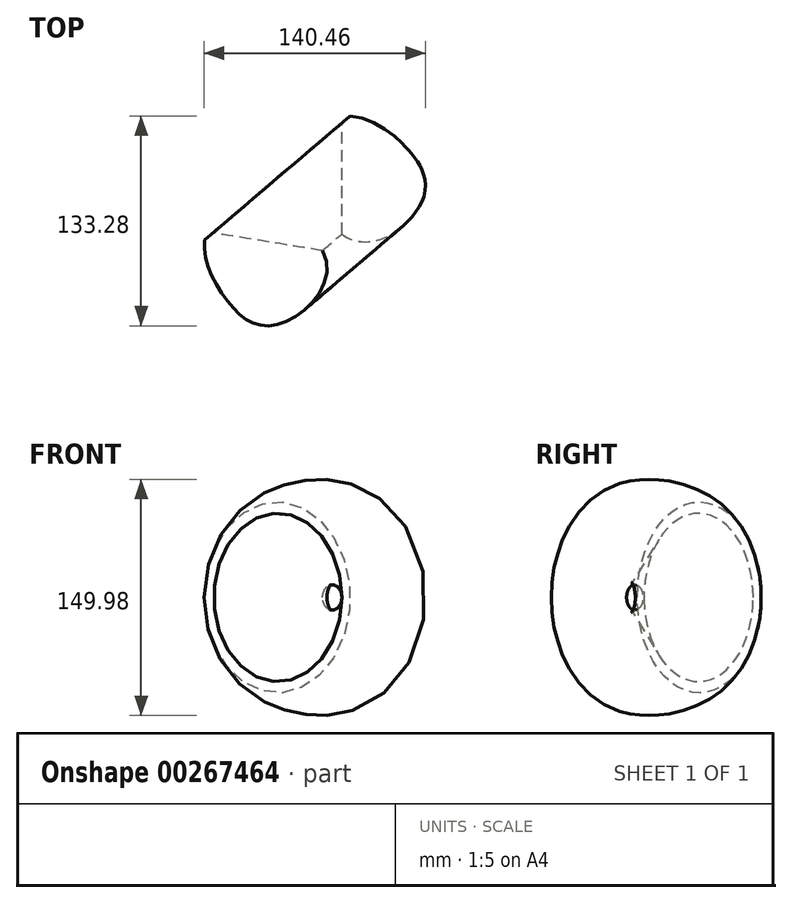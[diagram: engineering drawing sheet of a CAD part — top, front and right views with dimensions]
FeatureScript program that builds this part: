
annotation { "Feature Type Name" : "Feature", "Feature Type Description" : "" }
export const myFeature = defineFeature(function(context is Context, id is Id, definition is map)
    precondition{}
    {
        {
            var Q0;
            Q0=qCreatedBy(makeId("Top.planeOp"),FACE);
            var sketch = newSketch(context, id + "F0", { "sketchPlane" : qUnion([Q0])});
            skLineSegment(sketch, "E0", {"start": v(-57.24, -10.1) * mm, "end": v(-14.35, -60.44) * mm});
            skLineSegment(sketch, "E1", {"start": v(0, 9.67) * mm, "end": v(0, -64.88) * mm});
            skFitSpline(sketch, "E2", {"points": [v(0, -64.88) * mm, v(50.46, -45.05) * mm, v(41.86, -10.86) * mm, v(0, 9.67) * mm], "startDerivative": vector(153.28, -112.55) * mm, "endDerivative": vector(-121.14, -26.94) * mm});
            skSolve(sketch);
        }
        {
            var Q0;
            Q0 = qSketchRegion(id + "F0", true);
            var Q1;
            Q1=sQuery(id+"F0.wireOp",EDGE,"E0");
            revolve(context, id + "F1", {"entities" : qUnion([Q0]), "axis" : qUnion([Q1]), "revolveType" : RevolveType.FULL});
        }
        {
            var Q0;
            {var subQ0=sQuery(id+"F0.wireOp",EDGE,"E2");var subQ1=sQuery(id+"F0.wireOp",EDGE,"E1");Q0=makeQuery(id+"F1.opRevolve","SWEPT_EDGE",EDGE,{"disambiguationData":[OSD([subQ1,subQ0]),TDD([makeQuery(id+"F0.imprint","INTERSECT",VERTEX,{"disambiguationData":[OD(0.0)],"derivedFrom":[subQ1,subQ0]})])]});}
            chamfer(context, id + "F2", {"entities" : qUnion([Q0]), "width" : 5.08 * mm, "tangentPropagation" : true});
        }
    });
